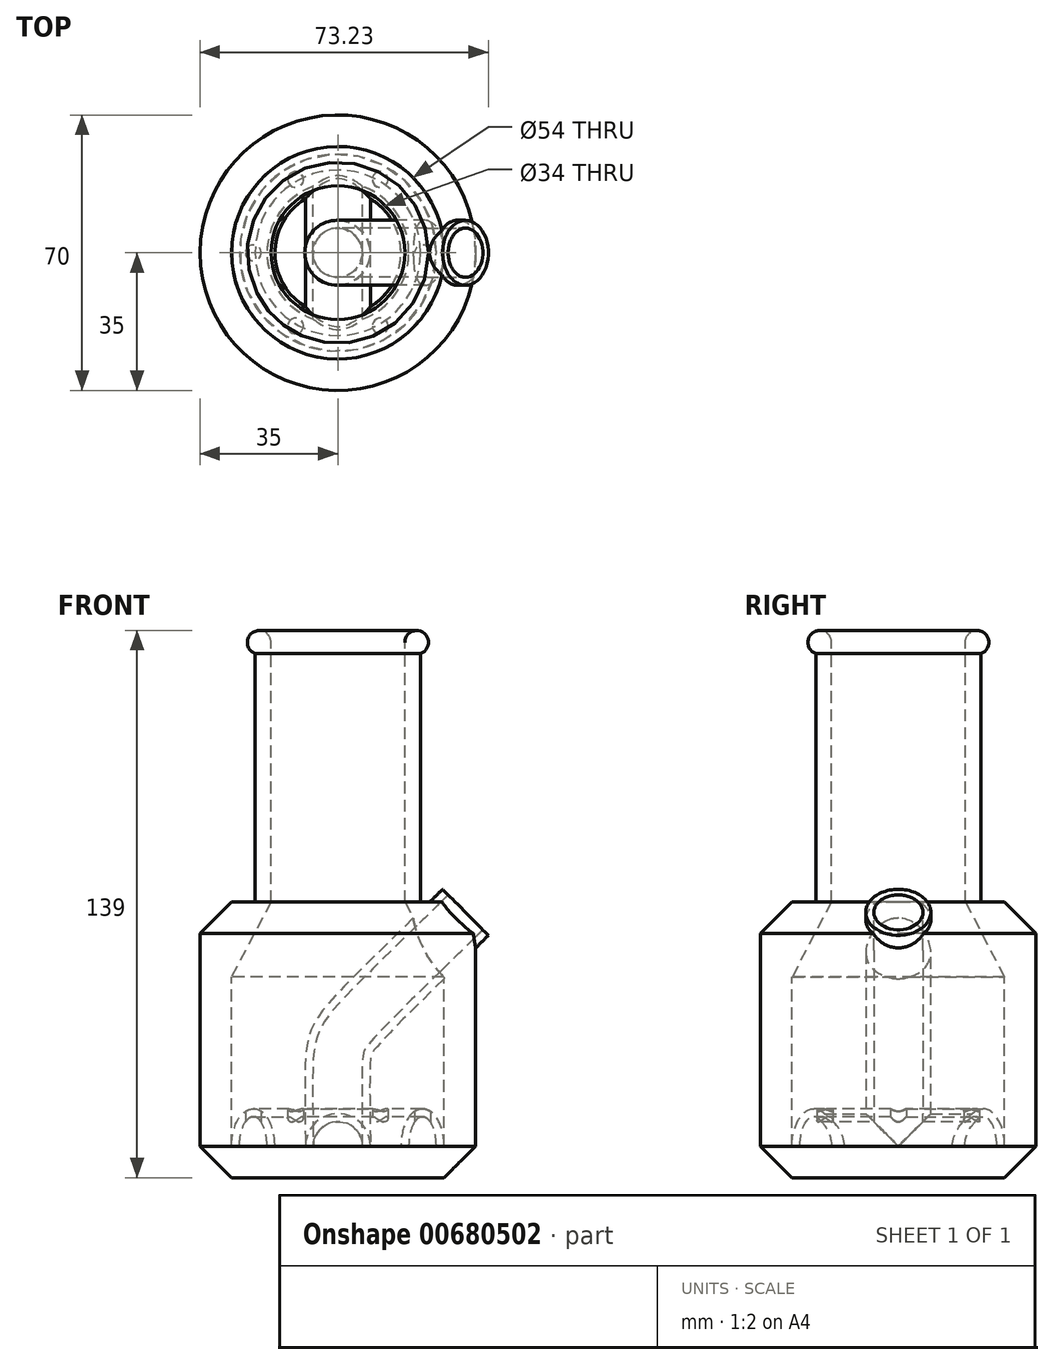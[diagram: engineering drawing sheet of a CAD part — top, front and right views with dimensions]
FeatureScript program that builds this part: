
annotation { "Feature Type Name" : "Feature", "Feature Type Description" : "" }
export const myFeature = defineFeature(function(context is Context, id is Id, definition is map)
    precondition{}
    {
        {
            var Q0;
            Q0=qCreatedBy(makeId("Front.planeOp"),FACE);
            var sketch = newSketch(context, id + "F0", { "sketchPlane" : qUnion([Q0])});
            skLineSegment(sketch, "E0", {"start": v(0, 209.04) * mm, "end": v(0, 0) * mm, "construction": true});
            skLineSegment(sketch, "E1", {"start": v(0, 0) * mm, "end": v(27, 0) * mm});
            skLineSegment(sketch, "E2", {"start": v(27, 0) * mm, "end": v(35, 8) * mm});
            skLineSegment(sketch, "E3", {"start": v(35, 8) * mm, "end": v(35, 62) * mm});
            skLineSegment(sketch, "E4", {"start": v(35, 62) * mm, "end": v(27, 70) * mm});
            skLineSegment(sketch, "E5", {"start": v(21, 70) * mm, "end": v(21, 133.17) * mm});
            skLineSegment(sketch, "E6", {"start": v(17, 136) * mm, "end": v(17, 70) * mm});
            skLineSegment(sketch, "E7", {"start": v(17, 70) * mm, "end": v(27, 51) * mm});
            skLineSegment(sketch, "E8", {"start": v(27, 51) * mm, "end": v(27, 8) * mm});
            skLineSegment(sketch, "E9", {"start": v(16, 8) * mm, "end": v(0, 8) * mm});
            skLineSegment(sketch, "E10", {"start": v(21, 70) * mm, "end": v(27, 70) * mm});
            skPoint(sketch, "E11", {"position": v(17, 136) * mm});
            skEllipticalArc(sketch, "E12", {});
            skLineSegment(sketch, "E13", {"start": v(0, 8) * mm, "end": v(0, 0) * mm});
            skEllipticalArc(sketch, "E14", {});
            skLineSegment(sketch, "E15", {"start": v(18, 8) * mm, "end": v(25, 8) * mm});
            skArc(sketch, "E16", {"start": v(21, 133.17) * mm, "mid": v(21.73, 138.45) * mm, "end": v(17, 136) * mm});
            skLineSegment(sketch, "E17", {"start": v(32.41, 67.41) * mm, "end": v(0, 35) * mm, "construction": true});
            skPoint(sketch, "E18", {"position": v(31, 66) * mm});
            skPoint(sketch, "E19", {"position": v(21.5, 15.5) * mm});
            skPoint(sketch, "E20", {"position": v(21.5, 17.5) * mm});
            const initialGuessF0  = {"E12": [0.0215, 0.008, 0, -1, 0.0095, 0.0055, 1.5707963267948966, 4.71238898038469], "E14": [0.0215, 0.008, 0, -1, 0.0075, 0.0035, 1.5707963267948966, 4.71238898038469]};
            skSetInitialGuess(sketch, initialGuessF0);
            skSolve(sketch);
        }
        {
            var Q0;
            Q0=makeQuery(id+"F0.imprint","IMPRINT",FACE,{"disambiguationData":[TD([[makeQuery(id+"F0.imprint","IMPRINT",EDGE,{"derivedFrom":sQuery(id+"F0.wireOp",EDGE,"E1")}),1.0]])]});
            var Q1;
            Q1=sQuery(id+"F0.wireOp",EDGE,"E0");
            revolve(context, id + "F1", {"surfaceOperationType" : NewSurfaceOperationType.NEW, "entities" : qUnion([Q0]), "axis" : qUnion([Q1]), "revolveType" : RevolveType.FULL});
        }
        {
            var Q0;
            Q0=qCreatedBy(makeId("Front.planeOp"),FACE);
            var sketch = newSketch(context, id + "F2", { "sketchPlane" : qUnion([Q0])});
            skFitSpline(sketch, "E21", {"points": [v(32.41, 67.41) * mm, v(3.66, 38.66) * mm, v(0.95, 34.6) * mm, v(0, 29.82) * mm, v(0, 8) * mm], "startDerivative": vector(-82.55, -81.94) * mm, "endDerivative": vector(0, -45.85) * mm});
            skPoint(sketch, "E22", {"position": v(12.5, 29.82) * mm});
            skLineSegment(sketch, "E23", {"start": v(12.5, 29.82) * mm, "end": v(3.66, 38.66) * mm, "construction": true});
            skLineSegment(sketch, "E24", {"start": v(0, 29.82) * mm, "end": v(12.5, 29.82) * mm, "construction": true});
            skLineSegment(sketch, "E25", {"start": v(12.5, 29.82) * mm, "end": v(0.95, 34.6) * mm, "construction": true});
            skSolve(sketch);
        }
        {
            var Q0;
            Q0=sQuery(id+"F2.wireOp",EDGE,"E21");
            var Q1;
            Q1=sQuery(id+"F2.wireOp",VERTEX,"E21.0.internal");
            cPlane(context, id + "F3", {"entities" : qUnion([Q0, Q1]), "cplaneType" : CPlaneType.CURVE_POINT, "offset" : 25 * mm, "width" : 150 * mm, "height" : 150 * mm});
        }
        {
            var Q0;
            Q0=qCreatedBy(id+"F3.planeOp",FACE);
            var sketch = newSketch(context, id + "F4", { "sketchPlane" : qUnion([Q0])});
            skCircle(sketch, "E26", {"center": v(0, 25.01) * mm, "radius": 6.25 * mm});
            skCircle(sketch, "E27", {"center": v(0, 25.01) * mm, "radius": 8.25 * mm});
            skSolve(sketch);
        }
        {
            var Q0;
            Q0=makeQuery(id+"F4.imprint","IMPRINT",FACE,{"disambiguationData":[TD([[makeQuery(id+"F4.imprint","IMPRINT",EDGE,{"derivedFrom":sQuery(id+"F4.wireOp",EDGE,"E26")}),-1.0]])]});
            var Q1;
            Q1=sQuery(id+"F2.wireOp",EDGE,"E21");
            sweep(context, id + "F5", {"operationType" : NewBodyOperationType.ADD, "profiles" : qUnion([Q0]), "path" : qUnion([Q1])});
        }
        {
            var Q0;
            Q0=qCreatedBy(makeId("Top.planeOp"),FACE);
            cPlane(context, id + "F6", {"entities" : qUnion([Q0]), "cplaneType" : CPlaneType.OFFSET, "offset" : 8 * mm, "width" : 150 * mm, "height" : 150 * mm});
        }
        {
            var Q0;
            Q0=qCreatedBy(id+"F6.planeOp",FACE);
            var sketch = newSketch(context, id + "F7", { "sketchPlane" : qUnion([Q0])});
            skLineSegment(sketch, "E28.bottom", {"start": v(0, -21.5) * mm, "end": v(8.25, -21.5) * mm});
            skLineSegment(sketch, "E28.top", {"start": v(0, 21.5) * mm, "end": v(8.25, 21.5) * mm});
            skLineSegment(sketch, "E28.left", {"start": v(0, -21.5) * mm, "end": v(0, 21.5) * mm});
            skLineSegment(sketch, "E28.right", {"start": v(8.25, -21.5) * mm, "end": v(8.25, 21.5) * mm});
            skLineSegment(sketch, "E29", {"start": v(6.25, -21.5) * mm, "end": v(6.25, 21.5) * mm});
            skSolve(sketch);
        }
        {
            var Q0;
            {var subQ0=sQuery(id+"F7.wireOp",EDGE,"E28.right");Q0=makeQuery(id+"F7.imprint","IMPRINT",FACE,{"disambiguationData":[TD([[makeQuery(id+"F7.imprint","IMPRINT",EDGE,{"derivedFrom":subQ0}),1.0]])]});}
            var Q1;
            Q1=sQuery(id+"F7.wireOp",EDGE,"E28.left");
            revolve(context, id + "F8", {"operationType" : NewBodyOperationType.ADD, "surfaceOperationType" : NewSurfaceOperationType.NEW, "entities" : qUnion([Q0]), "axis" : qUnion([Q1]), "revolveType" : RevolveType.ONE_DIRECTION, "oppositeDirection" : true, "angle" : 180 * degree});
        }
        {
            var Q0;
            Q0=qCreatedBy(makeId("Top.planeOp"),FACE);
            cPlane(context, id + "F9", {"entities" : qUnion([Q0]), "cplaneType" : CPlaneType.OFFSET, "offset" : 13 * mm, "width" : 150 * mm, "height" : 150 * mm});
        }
        {
            var Q0;
            Q0=qCreatedBy(id+"F9.planeOp",FACE);
            var sketch = newSketch(context, id + "F10", { "sketchPlane" : qUnion([Q0])});
            skCircle(sketch, "E30", {"center": v(21.5, 0) * mm, "radius": 2 * mm});
            skCircle(sketch, "E31.1.0", {"center": v(10.75, 18.62) * mm, "radius": 2 * mm});
            skCircle(sketch, "E31.2.0", {"center": v(-10.75, 18.62) * mm, "radius": 2 * mm});
            skCircle(sketch, "E31.3.0", {"center": v(-21.5, 0) * mm, "radius": 2 * mm});
            skCircle(sketch, "E31.4.0", {"center": v(-10.75, -18.62) * mm, "radius": 2 * mm});
            skCircle(sketch, "E31.5.0", {"center": v(10.75, -18.62) * mm, "radius": 2 * mm});
            skPoint(sketch, "E31.center", {"position": v(0, 0) * mm});
            skSolve(sketch);
        }
        {
            var Q0;
            Q0 = qSketchRegion(id + "F10", true);
            extrude(context, id + "F11", {"entities" : qUnion([Q0]), "operationType" : NewBodyOperationType.REMOVE, "depth" : 5 * mm, "offsetDistance" : 25 * mm});
        }
        {
            var Q0;
            Q0=makeQuery(id+"F0.imprint","IMPRINT",FACE,{"disambiguationData":[TD([[makeQuery(id+"F0.imprint","IMPRINT",EDGE,{"derivedFrom":sQuery(id+"F0.wireOp",EDGE,"E14")}),1.0]])]});
            var Q1;
            Q1=sQuery(id+"F0.wireOp",EDGE,"E0");
            revolve(context, id + "F12", {"operationType" : NewBodyOperationType.REMOVE, "surfaceOperationType" : NewSurfaceOperationType.NEW, "entities" : qUnion([Q0]), "axis" : qUnion([Q1]), "revolveType" : RevolveType.FULL, "oppositeDirection" : true});
        }
        {
            var Q0;
            {var subQ0=sQuery(id+"F7.wireOp",EDGE,"E28.left");Q0=makeQuery(id+"F7.imprint","IMPRINT",FACE,{"disambiguationData":[TD([[makeQuery(id+"F7.imprint","IMPRINT",EDGE,{"derivedFrom":subQ0}),-1.0]])]});}
            var Q1;
            Q1=sQuery(id+"F7.wireOp",EDGE,"E28.left");
            revolve(context, id + "F13", {"operationType" : NewBodyOperationType.REMOVE, "surfaceOperationType" : NewSurfaceOperationType.NEW, "entities" : qUnion([Q0]), "axis" : qUnion([Q1]), "revolveType" : RevolveType.ONE_DIRECTION, "oppositeDirection" : true, "angle" : 180 * degree});
        }
        {
            var Q0;
            Q0=makeQuery(id+"F4.imprint","IMPRINT",FACE,{"disambiguationData":[TD([[makeQuery(id+"F4.imprint","IMPRINT",EDGE,{"derivedFrom":sQuery(id+"F4.wireOp",EDGE,"E26")}),1.0]])]});
            var Q1;
            Q1=sQuery(id+"F2.wireOp",EDGE,"E21");
            sweep(context, id + "F14", {"operationType" : NewBodyOperationType.REMOVE, "profiles" : qUnion([Q0]), "path" : qUnion([Q1])});
        }
    });
